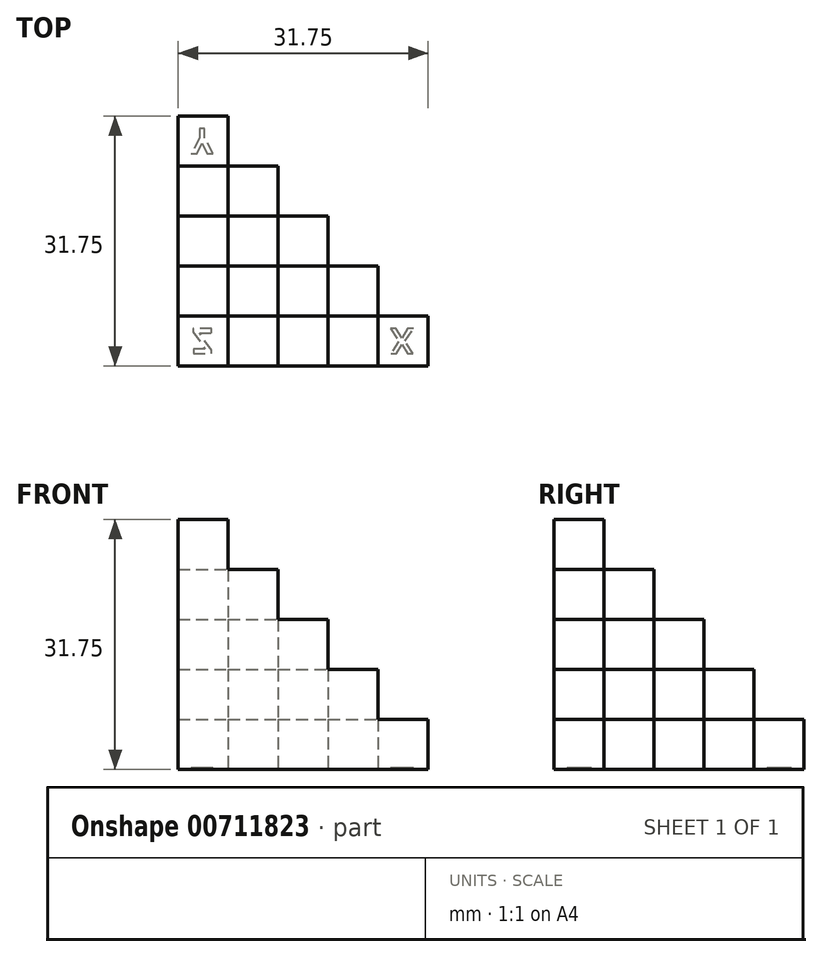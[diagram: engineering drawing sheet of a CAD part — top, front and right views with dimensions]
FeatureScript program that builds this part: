
annotation { "Feature Type Name" : "Feature", "Feature Type Description" : "" }
export const myFeature = defineFeature(function(context is Context, id is Id, definition is map)
    precondition{}
    {
        {
            assignVariable(context, id + "F0", {"name" : "Size", "anyValue" : 6.35 * mm});
        }
        {
            var Q0;
            Q0=qCreatedBy(makeId("Top.planeOp"),FACE);
            var sketch = newSketch(context, id + "F1", { "sketchPlane" : qUnion([Q0])});
            skLineSegment(sketch, "E0.bottom", {"start": v(0, 0) * mm, "end": v(6.35, 0) * mm});
            skLineSegment(sketch, "E0.top", {"start": v(0, 6.35) * mm, "end": v(6.35, 6.35) * mm});
            skLineSegment(sketch, "E0.left", {"start": v(0, 0) * mm, "end": v(0, 6.35) * mm});
            skLineSegment(sketch, "E0.right", {"start": v(6.35, 0) * mm, "end": v(6.35, 6.35) * mm});
            skLineSegment(sketch, "E1", {"start": v(6.35, 6.35) * mm, "end": v(12.7, 6.35) * mm});
            skLineSegment(sketch, "E2", {"start": v(12.7, 6.35) * mm, "end": v(12.7, 0) * mm});
            skLineSegment(sketch, "E3", {"start": v(12.7, 0) * mm, "end": v(6.35, 0) * mm});
            skLineSegment(sketch, "E4", {"start": v(12.7, 6.35) * mm, "end": v(19.05, 6.35) * mm});
            skLineSegment(sketch, "E5", {"start": v(19.05, 6.35) * mm, "end": v(19.05, 0) * mm});
            skLineSegment(sketch, "E6", {"start": v(19.05, 0) * mm, "end": v(12.7, 0) * mm});
            skLineSegment(sketch, "E7", {"start": v(19.05, 6.35) * mm, "end": v(25.4, 6.35) * mm});
            skLineSegment(sketch, "E8", {"start": v(25.4, 6.35) * mm, "end": v(25.4, 0) * mm});
            skLineSegment(sketch, "E9", {"start": v(25.4, 0) * mm, "end": v(19.05, 0) * mm});
            skLineSegment(sketch, "E10", {"start": v(25.4, 6.35) * mm, "end": v(31.75, 6.35) * mm});
            skLineSegment(sketch, "E11", {"start": v(31.75, 6.35) * mm, "end": v(31.75, 0) * mm});
            skLineSegment(sketch, "E12", {"start": v(31.75, 0) * mm, "end": v(25.4, 0) * mm});
            skLineSegment(sketch, "E13", {"start": v(0, 6.35) * mm, "end": v(0, 12.7) * mm});
            skLineSegment(sketch, "E14", {"start": v(0, 12.7) * mm, "end": v(6.35, 12.7) * mm});
            skLineSegment(sketch, "E15", {"start": v(6.35, 12.7) * mm, "end": v(6.35, 6.35) * mm});
            skLineSegment(sketch, "E16", {"start": v(0, 12.7) * mm, "end": v(0, 19.05) * mm});
            skLineSegment(sketch, "E17", {"start": v(0, 19.05) * mm, "end": v(6.35, 19.05) * mm});
            skLineSegment(sketch, "E18", {"start": v(6.35, 19.05) * mm, "end": v(6.35, 12.7) * mm});
            skLineSegment(sketch, "E19", {"start": v(0, 19.05) * mm, "end": v(0, 25.4) * mm});
            skLineSegment(sketch, "E20", {"start": v(0, 25.4) * mm, "end": v(6.35, 25.4) * mm});
            skLineSegment(sketch, "E21", {"start": v(6.35, 25.4) * mm, "end": v(6.35, 19.05) * mm});
            skLineSegment(sketch, "E22", {"start": v(0, 25.4) * mm, "end": v(0, 31.75) * mm});
            skLineSegment(sketch, "E23", {"start": v(0, 31.75) * mm, "end": v(6.35, 31.75) * mm});
            skLineSegment(sketch, "E24", {"start": v(6.35, 31.75) * mm, "end": v(6.35, 25.4) * mm});
            skLineSegment(sketch, "E25", {"start": v(6.35, 12.7) * mm, "end": v(12.7, 12.7) * mm});
            skLineSegment(sketch, "E26", {"start": v(12.7, 12.7) * mm, "end": v(12.7, 6.35) * mm});
            skLineSegment(sketch, "E27", {"start": v(12.7, 12.7) * mm, "end": v(19.05, 12.7) * mm});
            skLineSegment(sketch, "E28", {"start": v(19.05, 12.7) * mm, "end": v(19.05, 6.35) * mm});
            skLineSegment(sketch, "E29", {"start": v(6.35, 19.05) * mm, "end": v(12.7, 19.05) * mm});
            skLineSegment(sketch, "E30", {"start": v(12.7, 19.05) * mm, "end": v(12.7, 12.7) * mm});
            skLineSegment(sketch, "E31", {"start": v(12.7, 19.05) * mm, "end": v(19.05, 19.05) * mm});
            skLineSegment(sketch, "E32", {"start": v(19.05, 19.05) * mm, "end": v(19.05, 12.7) * mm});
            skLineSegment(sketch, "E33", {"start": v(6.35, 25.4) * mm, "end": v(12.7, 25.4) * mm});
            skLineSegment(sketch, "E34", {"start": v(12.7, 25.4) * mm, "end": v(12.7, 19.05) * mm});
            skLineSegment(sketch, "E35", {"start": v(19.05, 12.7) * mm, "end": v(25.4, 12.7) * mm});
            skLineSegment(sketch, "E36", {"start": v(25.4, 12.7) * mm, "end": v(25.4, 6.35) * mm});
            skSolve(sketch);
        }
        {
            var Q0;
            Q0=makeQuery(id+"F1.imprint","IMPRINT",FACE,{"disambiguationData":[TD([[makeQuery(id+"F1.imprint","IMPRINT",EDGE,{"derivedFrom":sQuery(id+"F1.wireOp",EDGE,"E0.bottom")}),1.0]])]});
            extrude(context, id + "F2", {"entities" : qUnion([Q0]), "depth" : 5 * getVariable(context, 'Size'), "offsetDistance" : 25.4 * mm});
        }
        {
            var Q0;
            Q0=makeQuery(id+"F1.imprint","IMPRINT",FACE,{"disambiguationData":[TD([[makeQuery(id+"F1.imprint","IMPRINT",EDGE,{"derivedFrom":sQuery(id+"F1.wireOp",EDGE,"E0.top")}),1.0]])]});
            var Q1;
            Q1=makeQuery(id+"F1.imprint","IMPRINT",FACE,{"disambiguationData":[TD([[makeQuery(id+"F1.imprint","IMPRINT",EDGE,{"derivedFrom":sQuery(id+"F1.wireOp",EDGE,"E0.right")}),-1.0]])]});
            extrude(context, id + "F3", {"entities" : qUnion([Q0, Q1]), "operationType" : NewBodyOperationType.ADD, "depth" : 4 * getVariable(context, 'Size'), "offsetDistance" : 25.4 * mm});
        }
        {
            var Q0;
            Q0=makeQuery(id+"F1.imprint","IMPRINT",FACE,{"disambiguationData":[TD([[makeQuery(id+"F1.imprint","IMPRINT",EDGE,{"derivedFrom":sQuery(id+"F1.wireOp",EDGE,"E14")}),1.0]])]});
            var Q1;
            Q1=makeQuery(id+"F1.imprint","IMPRINT",FACE,{"disambiguationData":[TD([[makeQuery(id+"F1.imprint","IMPRINT",EDGE,{"derivedFrom":sQuery(id+"F1.wireOp",EDGE,"E1")}),1.0]])]});
            var Q2;
            Q2=makeQuery(id+"F1.imprint","IMPRINT",FACE,{"disambiguationData":[TD([[makeQuery(id+"F1.imprint","IMPRINT",EDGE,{"derivedFrom":sQuery(id+"F1.wireOp",EDGE,"E2")}),1.0]])]});
            extrude(context, id + "F4", {"entities" : qUnion([Q0, Q1, Q2]), "operationType" : NewBodyOperationType.ADD, "depth" : 3 * getVariable(context, 'Size'), "offsetDistance" : 25.4 * mm});
        }
        {
            var Q0;
            Q0=makeQuery(id+"F1.imprint","IMPRINT",FACE,{"disambiguationData":[TD([[makeQuery(id+"F1.imprint","IMPRINT",EDGE,{"derivedFrom":sQuery(id+"F1.wireOp",EDGE,"E17")}),1.0]])]});
            var Q1;
            Q1=makeQuery(id+"F1.imprint","IMPRINT",FACE,{"disambiguationData":[TD([[makeQuery(id+"F1.imprint","IMPRINT",EDGE,{"derivedFrom":sQuery(id+"F1.wireOp",EDGE,"E18")}),1.0]])]});
            var Q2;
            Q2=makeQuery(id+"F1.imprint","IMPRINT",FACE,{"disambiguationData":[TD([[makeQuery(id+"F1.imprint","IMPRINT",EDGE,{"derivedFrom":sQuery(id+"F1.wireOp",EDGE,"E4")}),1.0]])]});
            var Q3;
            Q3=makeQuery(id+"F1.imprint","IMPRINT",FACE,{"disambiguationData":[TD([[makeQuery(id+"F1.imprint","IMPRINT",EDGE,{"derivedFrom":sQuery(id+"F1.wireOp",EDGE,"E5")}),1.0]])]});
            extrude(context, id + "F5", {"entities" : qUnion([Q0, Q1, Q2, Q3]), "operationType" : NewBodyOperationType.ADD, "depth" : 2 * getVariable(context, 'Size'), "offsetDistance" : 25.4 * mm});
        }
        {
            var Q0;
            Q0=makeQuery(id+"F1.imprint","IMPRINT",FACE,{"disambiguationData":[TD([[makeQuery(id+"F1.imprint","IMPRINT",EDGE,{"derivedFrom":sQuery(id+"F1.wireOp",EDGE,"E20")}),1.0]])]});
            var Q1;
            Q1=makeQuery(id+"F1.imprint","IMPRINT",FACE,{"disambiguationData":[TD([[makeQuery(id+"F1.imprint","IMPRINT",EDGE,{"derivedFrom":sQuery(id+"F1.wireOp",EDGE,"E21")}),1.0]])]});
            var Q2;
            Q2=makeQuery(id+"F1.imprint","IMPRINT",FACE,{"disambiguationData":[TD([[makeQuery(id+"F1.imprint","IMPRINT",EDGE,{"derivedFrom":sQuery(id+"F1.wireOp",EDGE,"E27")}),1.0]])]});
            var Q3;
            Q3=makeQuery(id+"F1.imprint","IMPRINT",FACE,{"disambiguationData":[TD([[makeQuery(id+"F1.imprint","IMPRINT",EDGE,{"derivedFrom":sQuery(id+"F1.wireOp",EDGE,"E7")}),1.0]])]});
            var Q4;
            Q4=makeQuery(id+"F1.imprint","IMPRINT",FACE,{"disambiguationData":[TD([[makeQuery(id+"F1.imprint","IMPRINT",EDGE,{"derivedFrom":sQuery(id+"F1.wireOp",EDGE,"E8")}),1.0]])]});
            extrude(context, id + "F6", {"entities" : qUnion([Q0, Q1, Q2, Q3, Q4]), "operationType" : NewBodyOperationType.ADD, "depth" : 1 * getVariable(context, 'Size'), "offsetDistance" : 25.4 * mm});
        }
        {
            var Q0;
            {var subQ0=sQuery(id+"F1.wireOp",EDGE,"E30");var subQ1=sQuery(id+"F1.wireOp",EDGE,"E27");var subQ2=sQuery(id+"F1.wireOp",EDGE,"E29");var subQ3=sQuery(id+"F1.wireOp",EDGE,"E21");var subQ4=sQuery(id+"F1.wireOp",EDGE,"E20");var subQ5=sQuery(id+"F1.wireOp",EDGE,"E8");var subQ6=sQuery(id+"F1.wireOp",EDGE,"E28");var subQ7=sQuery(id+"F1.wireOp",EDGE,"E7");var subQ8=sQuery(id+"F1.wireOp",EDGE,"E25");var subQ9=sQuery(id+"F1.wireOp",EDGE,"E18");var subQ10=sQuery(id+"F1.wireOp",EDGE,"E17");var subQ11=sQuery(id+"F1.wireOp",EDGE,"E5");var subQ12=sQuery(id+"F1.wireOp",EDGE,"E26");var subQ13=sQuery(id+"F1.wireOp",EDGE,"E4");var subQ14=sQuery(id+"F1.wireOp",EDGE,"E14");var subQ15=sQuery(id+"F1.wireOp",EDGE,"E2");var subQ16=sQuery(id+"F1.wireOp",EDGE,"E15");var subQ17=sQuery(id+"F1.wireOp",EDGE,"E1");var subQ18=sQuery(id+"F1.wireOp",EDGE,"E0.right");var subQ19=sQuery(id+"F1.wireOp",EDGE,"E0.top");Q0=makeQuery(id+"F6.boolean.opBoolean","MERGE",FACE,{"derivedFrom":[makeQuery(id+"F5.boolean.opBoolean","MERGE",FACE,{"derivedFrom":[makeQuery(id+"F4.boolean.opBoolean","MERGE",FACE,{"derivedFrom":[makeQuery(id+"F3.boolean.opBoolean","MERGE",FACE,{"derivedFrom":[makeQuery(id+"F2.opExtrude","CAP_FACE",FACE,{"disambiguationData":[OSD([sQuery(id+"F1.wireOp",EDGE,"E0.bottom"),subQ19,sQuery(id+"F1.wireOp",EDGE,"E0.left"),subQ18])],"isStart":true}),makeQuery(id+"F3.opExtrude","CAP_FACE",FACE,{"disambiguationData":[OSD([subQ19,sQuery(id+"F1.wireOp",EDGE,"E13"),subQ14,subQ16])],"isStart":true}),makeQuery(id+"F3.opExtrude","CAP_FACE",FACE,{"disambiguationData":[OSD([subQ18,subQ17,subQ15,sQuery(id+"F1.wireOp",EDGE,"E3")])],"isStart":true})]}),makeQuery(id+"F4.opExtrude","CAP_FACE",FACE,{"disambiguationData":[OSD([subQ17,subQ16,subQ8,subQ12])],"isStart":true}),makeQuery(id+"F4.opExtrude","CAP_FACE",FACE,{"disambiguationData":[OSD([subQ15,subQ13,subQ11,sQuery(id+"F1.wireOp",EDGE,"E6")])],"isStart":true}),makeQuery(id+"F4.opExtrude","CAP_FACE",FACE,{"disambiguationData":[OSD([subQ14,sQuery(id+"F1.wireOp",EDGE,"E16"),subQ10,subQ9])],"isStart":true})]}),makeQuery(id+"F5.opExtrude","CAP_FACE",FACE,{"disambiguationData":[OSD([subQ13,subQ12,subQ1,subQ6])],"isStart":true}),makeQuery(id+"F5.opExtrude","CAP_FACE",FACE,{"disambiguationData":[OSD([subQ11,subQ7,subQ5,sQuery(id+"F1.wireOp",EDGE,"E9")])],"isStart":true}),makeQuery(id+"F5.opExtrude","CAP_FACE",FACE,{"disambiguationData":[OSD([subQ10,sQuery(id+"F1.wireOp",EDGE,"E19"),subQ4,subQ3])],"isStart":true}),makeQuery(id+"F5.opExtrude","CAP_FACE",FACE,{"disambiguationData":[OSD([subQ9,subQ8,subQ2,subQ0])],"isStart":true})]}),makeQuery(id+"F6.opExtrude","CAP_FACE",FACE,{"disambiguationData":[OSD([subQ7,subQ6,sQuery(id+"F1.wireOp",EDGE,"E35"),sQuery(id+"F1.wireOp",EDGE,"E36")])],"isStart":true}),makeQuery(id+"F6.opExtrude","CAP_FACE",FACE,{"disambiguationData":[OSD([subQ5,sQuery(id+"F1.wireOp",EDGE,"E10"),sQuery(id+"F1.wireOp",EDGE,"E11"),sQuery(id+"F1.wireOp",EDGE,"E12")])],"isStart":true}),makeQuery(id+"F6.opExtrude","CAP_FACE",FACE,{"disambiguationData":[OSD([subQ4,sQuery(id+"F1.wireOp",EDGE,"E22"),sQuery(id+"F1.wireOp",EDGE,"E23"),sQuery(id+"F1.wireOp",EDGE,"E24")])],"isStart":true}),makeQuery(id+"F6.opExtrude","CAP_FACE",FACE,{"disambiguationData":[OSD([subQ3,subQ2,sQuery(id+"F1.wireOp",EDGE,"E33"),sQuery(id+"F1.wireOp",EDGE,"E34")])],"isStart":true}),makeQuery(id+"F6.opExtrude","CAP_FACE",FACE,{"disambiguationData":[OSD([subQ1,subQ0,sQuery(id+"F1.wireOp",EDGE,"E31"),sQuery(id+"F1.wireOp",EDGE,"E32")])],"isStart":true})]});}
            var sketch = newSketch(context, id + "F7", { "sketchPlane" : qUnion([Q0])});
            skText(sketch, "E37", { "text": "Y", "fontName": "OpenSans-Bold.ttf"});
            skText(sketch, "E38", { "text": "Z", "fontName": "OpenSans-Bold.ttf"});
            skText(sketch, "E39", { "text": "X", "fontName": "OpenSans-Bold.ttf"});
            skPoint(sketch, "E40", {"position": v(28.58, -3.18) * mm});
            skPoint(sketch, "E41", {"position": v(3.18, -28.58) * mm});
            skPoint(sketch, "E42", {"position": v(3.17, -3.18) * mm});
            const initialGuessF7  = {"E37": [0.00166, -0.03016, 1, 0, 0.00318], "E38": [0.0018, -0.00476, 1, 0, 0.00318], "E39": [0.02696, -0.00476, 1, 0, 0.00318]};
            skSetInitialGuess(sketch, initialGuessF7);
            skSolve(sketch);
        }
        {
            var Q0;
            Q0 = qSketchRegion(id + "F7", true);
            extrude(context, id + "F8", {"entities" : qUnion([Q0]), "operationType" : NewBodyOperationType.REMOVE, "oppositeDirection" : true, "depth" : .2 * mm, "offsetDistance" : 25.4 * mm});
        }
    });
